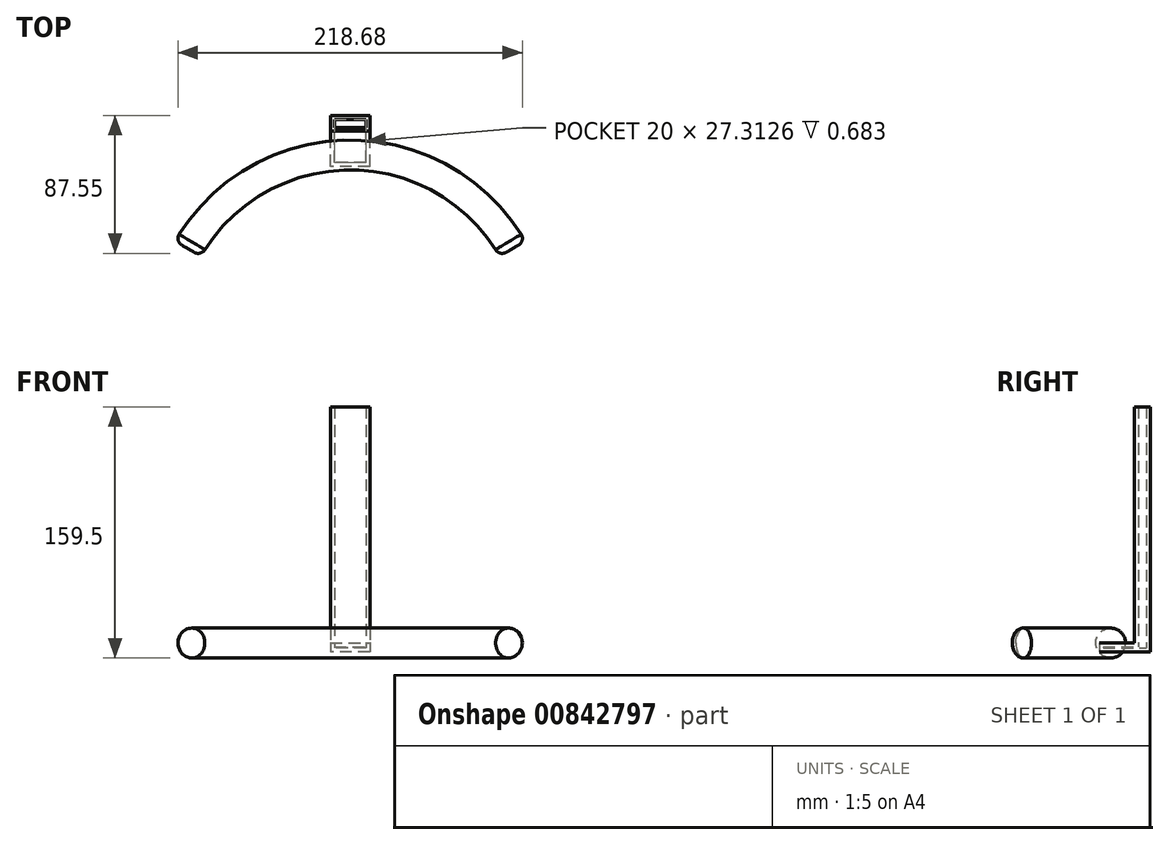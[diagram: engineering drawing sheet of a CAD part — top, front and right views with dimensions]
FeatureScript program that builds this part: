
annotation { "Feature Type Name" : "Feature", "Feature Type Description" : "" }
export const myFeature = defineFeature(function(context is Context, id is Id, definition is map)
    precondition{}
    {
        {
            var Q0;
            Q0=qCreatedBy(makeId("Right.planeOp"),FACE);
            var sketch = newSketch(context, id + "F0", { "sketchPlane" : qUnion([Q0])});
            skCircle(sketch, "E0", {"center": v(27.76, 0) * mm, "radius": 9.5 * mm});
            skLineSegment(sketch, "E1", {"start": v(-91.22, 37.36) * mm, "end": v(-91.22, -34) * mm});
            skSolve(sketch);
        }
        {
            var Q0;
            Q0=makeQuery(id+"F0.imprint","IMPRINT",FACE,{"disambiguationData":[TD([[makeQuery(id+"F0.imprint","IMPRINT",EDGE,{"derivedFrom":sQuery(id+"F0.wireOp",EDGE,"E0")}),1.0]])]});
            var Q1;
            Q1=sQuery(id+"F0.wireOp",EDGE,"E0");
            var Q2;
            Q2=sQuery(id+"F0.wireOp",EDGE,"E1");
            revolve(context, id + "F1", {"surfaceOperationType" : NewSurfaceOperationType.NEW, "entities" : qUnion([Q0]), "surfaceEntities" : qUnion([Q1]), "axis" : qUnion([Q2]), "revolveType" : RevolveType.SYMMETRIC, "angle" : 120 * degree});
        }
        {
            var Q0;
            Q0=qCreatedBy(makeId("Right.planeOp"),FACE);
            var sketch = newSketch(context, id + "F2", { "sketchPlane" : qUnion([Q0])});
            skLineSegment(sketch, "E2.bottom", {"start": v(20.54, 0) * mm, "end": v(52.85, 0) * mm});
            skLineSegment(sketch, "E2.top", {"start": v(20.54, -5.68) * mm, "end": v(52.85, -5.68) * mm});
            skLineSegment(sketch, "E2.left", {"start": v(20.54, 0) * mm, "end": v(20.54, -5.68) * mm});
            skLineSegment(sketch, "E2.right", {"start": v(52.85, 0) * mm, "end": v(52.85, -5.68) * mm});
            skSolve(sketch);
        }
        {
            var Q0;
            Q0 = qSketchRegion(id + "F2", true);
            extrude(context, id + "F3", {"entities" : qUnion([Q0]), "endBound" : BoundingType.SYMMETRIC, "depth" : 25 * mm, "offsetDistance" : 25 * mm});
        }
        {
            var Q0;
            Q0=makeQuery(id+"F3.opExtrude","SWEPT_FACE",FACE,{"disambiguationData":[OSD([sQuery(id+"F2.wireOp",EDGE,"E2.bottom")])]});
            var sketch = newSketch(context, id + "F4", { "sketchPlane" : qUnion([Q0])});
            skLineSegment(sketch, "E3.bottom", {"start": v(-12.5, 42.85) * mm, "end": v(12.5, 42.85) * mm});
            skLineSegment(sketch, "E3.top", {"start": v(-12.5, 52.85) * mm, "end": v(12.5, 52.85) * mm});
            skLineSegment(sketch, "E3.left", {"start": v(-12.5, 42.85) * mm, "end": v(-12.5, 52.85) * mm});
            skLineSegment(sketch, "E3.right", {"start": v(12.5, 42.85) * mm, "end": v(12.5, 52.85) * mm});
            skSolve(sketch);
        }
        {
            var Q0;
            Q0=makeQuery(id+"F4.imprint","IMPRINT",FACE,{"disambiguationData":[TD([[makeQuery(id+"F4.imprint","IMPRINT",EDGE,{"derivedFrom":sQuery(id+"F4.wireOp",EDGE,"E3.bottom")}),1.0]])]});
            extrude(context, id + "F5", {"entities" : qUnion([Q0]), "operationType" : NewBodyOperationType.ADD, "depth" : 150 * mm, "offsetDistance" : 25 * mm});
        }
        {
            var Q0;
            Q0=makeQuery(id+"F5.opExtrude","CAP_FACE",FACE,{"disambiguationData":[OSD([sQuery(id+"F4.wireOp",EDGE,"E3.bottom"),sQuery(id+"F4.wireOp",EDGE,"E3.top"),sQuery(id+"F4.wireOp",EDGE,"E3.left"),sQuery(id+"F4.wireOp",EDGE,"E3.right")])],"isStart":false});
            shell(context, id + "F6", {"entities" : qUnion([Q0]), "thickness" : 2.5 * mm});
        }
        {
            var Q0;
            Q0=makeQuery(id+"F1.opRevolve","SWEPT_FACE",FACE,{"disambiguationData":[OSD([sQuery(id+"F0.wireOp",EDGE,"E0")])]});
            fillet(context, id + "F7", {"entities" : qUnion([Q0]), "radius" : 5 * mm, "tangentPropagation" : true, "allowEdgeOverflow" : false});
        }
    });
